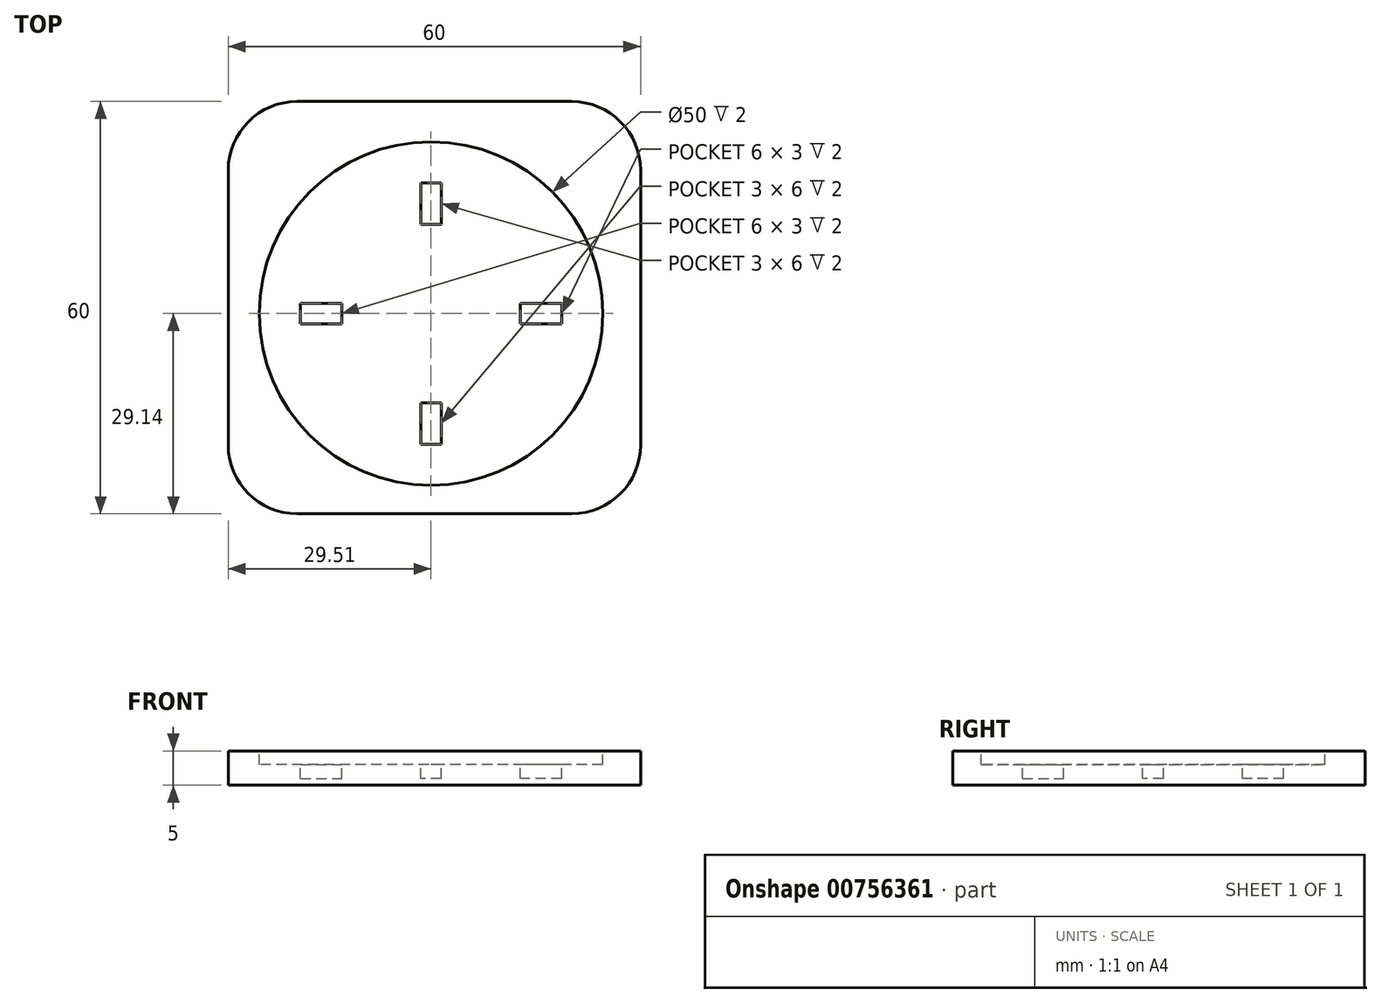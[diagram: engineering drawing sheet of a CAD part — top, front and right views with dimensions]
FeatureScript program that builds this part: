
annotation { "Feature Type Name" : "Feature", "Feature Type Description" : "" }
export const myFeature = defineFeature(function(context is Context, id is Id, definition is map)
    precondition{}
    {
        {
            var Q0;
            Q0=qCreatedBy(makeId("Top.planeOp"),FACE);
            var sketch = newSketch(context, id + "F0", { "sketchPlane" : qUnion([Q0])});
            skLineSegment(sketch, "E0.bottom", {"start": v(-29.51, 30.86) * mm, "end": v(30.49, 30.86) * mm});
            skLineSegment(sketch, "E0.top", {"start": v(-29.51, -29.14) * mm, "end": v(30.49, -29.14) * mm});
            skLineSegment(sketch, "E0.left", {"start": v(-29.51, 30.86) * mm, "end": v(-29.51, -29.14) * mm});
            skLineSegment(sketch, "E0.right", {"start": v(30.49, 30.86) * mm, "end": v(30.49, -29.14) * mm});
            skSolve(sketch);
        }
        {
            var Q0;
            Q0 = qSketchRegion(id + "F0", true);
            extrude(context, id + "F1", {"entities" : qUnion([Q0]), "depth" : 5 * mm, "offsetDistance" : 25 * mm});
        }
        {
            var Q0;
            Q0=makeQuery(id+"F1.opExtrude","CAP_FACE",FACE,{"disambiguationData":[OSD([sQuery(id+"F0.wireOp",EDGE,"E0.bottom"),sQuery(id+"F0.wireOp",EDGE,"E0.top"),sQuery(id+"F0.wireOp",EDGE,"E0.left"),sQuery(id+"F0.wireOp",EDGE,"E0.right")])],"isStart":false});
            var sketch = newSketch(context, id + "F2", { "sketchPlane" : qUnion([Q0])});
            skCircle(sketch, "E1", {"center": v(0, 0) * mm, "radius": 25 * mm});
            skSolve(sketch);
        }
        {
            var Q0;
            Q0 = qSketchRegion(id + "F2", true);
            extrude(context, id + "F3", {"entities" : qUnion([Q0]), "operationType" : NewBodyOperationType.REMOVE, "oppositeDirection" : true, "depth" : 2 * mm, "offsetDistance" : 25 * mm});
        }
        {
            var Q0;
            Q0=makeQuery(id+"F1.opExtrude","SWEPT_EDGE",EDGE,{"disambiguationData":[OSD([sQuery(id+"F0.wireOp",EDGE,"E0.bottom"),sQuery(id+"F0.wireOp",EDGE,"E0.right")])]});
            var Q1;
            Q1=makeQuery(id+"F1.opExtrude","SWEPT_EDGE",EDGE,{"disambiguationData":[OSD([sQuery(id+"F0.wireOp",EDGE,"E0.top"),sQuery(id+"F0.wireOp",EDGE,"E0.right")])]});
            var Q2;
            Q2=makeQuery(id+"F1.opExtrude","SWEPT_EDGE",EDGE,{"disambiguationData":[OSD([sQuery(id+"F0.wireOp",EDGE,"E0.top"),sQuery(id+"F0.wireOp",EDGE,"E0.left")])]});
            var Q3;
            Q3=makeQuery(id+"F1.opExtrude","SWEPT_EDGE",EDGE,{"disambiguationData":[OSD([sQuery(id+"F0.wireOp",EDGE,"E0.bottom"),sQuery(id+"F0.wireOp",EDGE,"E0.left")])]});
            fillet(context, id + "F4", {"entities" : qUnion([Q0, Q1, Q2, Q3]), "radius" : 10 * mm, "tangentPropagation" : true, "allowEdgeOverflow" : false});
        }
        {
            var Q0;
            Q0=makeQuery(id+"F3.boolean.opBoolean","COPY",FACE,{"derivedFrom":makeQuery(id+"F3.opExtrude","CAP_FACE",FACE,{"disambiguationData":[OSD([sQuery(id+"F2.wireOp",EDGE,"E1")])],"isStart":false})});
            var sketch = newSketch(context, id + "F5", { "sketchPlane" : qUnion([Q0])});
            skLineSegment(sketch, "E2.bottom", {"start": v(-1.5, 19) * mm, "end": v(1.5, 19) * mm});
            skLineSegment(sketch, "E2.top", {"start": v(-1.5, 13) * mm, "end": v(1.5, 13) * mm});
            skLineSegment(sketch, "E2.left", {"start": v(-1.5, 19) * mm, "end": v(-1.5, 13) * mm});
            skLineSegment(sketch, "E2.right", {"start": v(1.5, 19) * mm, "end": v(1.5, 13) * mm});
            skPoint(sketch, "E2.middle", {"position": v(0, 16) * mm});
            skLineSegment(sketch, "E3.1.0", {"start": v(-13, -1.5) * mm, "end": v(-13, 1.5) * mm});
            skLineSegment(sketch, "E3.1.1", {"start": v(-19, 1.5) * mm, "end": v(-13, 1.5) * mm});
            skLineSegment(sketch, "E3.1.2", {"start": v(-19, -1.5) * mm, "end": v(-19, 1.5) * mm});
            skLineSegment(sketch, "E3.1.3", {"start": v(-19, -1.5) * mm, "end": v(-13, -1.5) * mm});
            skLineSegment(sketch, "E3.2.0", {"start": v(1.5, -13) * mm, "end": v(-1.5, -13) * mm});
            skLineSegment(sketch, "E3.2.1", {"start": v(-1.5, -19) * mm, "end": v(-1.5, -13) * mm});
            skLineSegment(sketch, "E3.2.2", {"start": v(1.5, -19) * mm, "end": v(-1.5, -19) * mm});
            skLineSegment(sketch, "E3.2.3", {"start": v(1.5, -19) * mm, "end": v(1.5, -13) * mm});
            skLineSegment(sketch, "E3.3.0", {"start": v(13, 1.5) * mm, "end": v(13, -1.5) * mm});
            skLineSegment(sketch, "E3.3.1", {"start": v(19, -1.5) * mm, "end": v(13, -1.5) * mm});
            skLineSegment(sketch, "E3.3.2", {"start": v(19, 1.5) * mm, "end": v(19, -1.5) * mm});
            skLineSegment(sketch, "E3.3.3", {"start": v(19, 1.5) * mm, "end": v(13, 1.5) * mm});
            skPoint(sketch, "E3.center", {"position": v(0, 0) * mm});
            skSolve(sketch);
        }
        {
            var Q0;
            Q0 = qSketchRegion(id + "F5", true);
            extrude(context, id + "F6", {"entities" : qUnion([Q0]), "operationType" : NewBodyOperationType.REMOVE, "oppositeDirection" : true, "depth" : 2 * mm, "offsetDistance" : 25 * mm});
        }
    });
